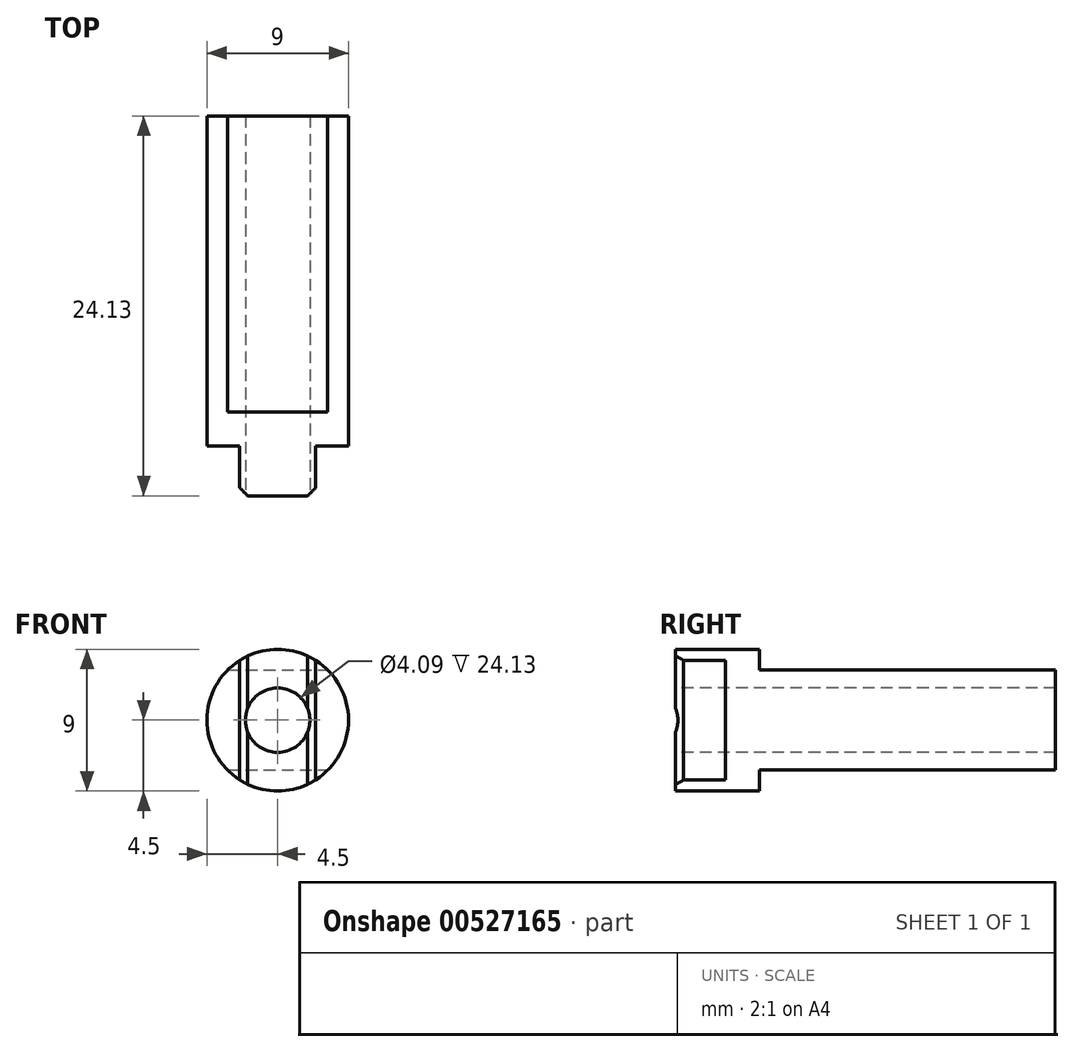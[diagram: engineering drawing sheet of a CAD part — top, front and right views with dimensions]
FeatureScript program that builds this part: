
annotation { "Feature Type Name" : "Feature", "Feature Type Description" : "" }
export const myFeature = defineFeature(function(context is Context, id is Id, definition is map)
    precondition{}
    {
        {
            var Q0;
            Q0=qCreatedBy(makeId("Front.planeOp"),FACE);
            var sketch = newSketch(context, id + "F0", { "sketchPlane" : qUnion([Q0])});
            skCircle(sketch, "E0", {"center": v(0, 0) * mm, "radius": 4.5 * mm});
            skSolve(sketch);
        }
        {
            var Q0;
            Q0=makeQuery(id+"F0.imprint","IMPRINT",FACE,{"disambiguationData":[TD([[makeQuery(id+"F0.imprint","IMPRINT",EDGE,{"derivedFrom":sQuery(id+"F0.wireOp",EDGE,"E0")}),1.0]])]});
            extrude(context, id + "F1", {"entities" : qUnion([Q0]), "oppositeDirection" : true, "depth" : 24.13 * mm, "offsetDistance" : 25.4 * mm});
        }
        {
            var Q0;
            Q0=qCreatedBy(makeId("Front.planeOp"),FACE);
            cPlane(context, id + "F2", {"entities" : qUnion([Q0]), "cplaneType" : CPlaneType.OFFSET, "offset" : 2.54 * mm, "width" : 152.4 * mm, "height" : 152.4 * mm});
        }
        {
            var Q0;
            Q0=qCreatedBy(id+"F2.planeOp",FACE);
            var sketch = newSketch(context, id + "F3", { "sketchPlane" : qUnion([Q0])});
            skLineSegment(sketch, "E1", {"start": v(-2.41, 9.78) * mm, "end": v(-2.41, -11.4) * mm});
            skLineSegment(sketch, "E2", {"start": v(-2.41, -11.4) * mm, "end": v(-8.76, -11.4) * mm});
            skLineSegment(sketch, "E3", {"start": v(-8.76, -11.4) * mm, "end": v(-8.76, 9.78) * mm});
            skLineSegment(sketch, "E4", {"start": v(-8.76, 9.78) * mm, "end": v(-2.41, 9.78) * mm});
            skLineSegment(sketch, "E5.MirrorCS", {"start": v(8.76, 9.78) * mm, "end": v(2.41, 9.78) * mm});
            skLineSegment(sketch, "E6.MirrorCS", {"start": v(8.76, -11.4) * mm, "end": v(8.76, 9.78) * mm});
            skLineSegment(sketch, "E7.MirrorCS", {"start": v(2.41, -11.4) * mm, "end": v(8.76, -11.4) * mm});
            skLineSegment(sketch, "E8.MirrorCS", {"start": v(2.41, 9.78) * mm, "end": v(2.41, -11.4) * mm});
            skSolve(sketch);
        }
        {
            var Q0;
            Q0=makeQuery(id+"F3.imprint","IMPRINT",FACE,{"disambiguationData":[TD([[makeQuery(id+"F3.imprint","IMPRINT",EDGE,{"derivedFrom":sQuery(id+"F3.wireOp",EDGE,"E1")}),-1.0]])]});
            var Q1;
            Q1=makeQuery(id+"F3.imprint","IMPRINT",FACE,{"disambiguationData":[TD([[makeQuery(id+"F3.imprint","IMPRINT",EDGE,{"derivedFrom":sQuery(id+"F3.wireOp",EDGE,"E5.MirrorCS")}),1.0]])]});
            extrude(context, id + "F4", {"entities" : qUnion([Q0, Q1]), "operationType" : NewBodyOperationType.REMOVE, "oppositeDirection" : true, "depth" : 5.7 * mm, "offsetDistance" : 25.4 * mm});
        }
        {
            var Q0;
            Q0=makeQuery(id+"F4.boolean.opBoolean","INTERSECT",EDGE,{"derivedFrom":[makeQuery(id+"F1.opExtrude","CAP_FACE",FACE,{"disambiguationData":[OSD([sQuery(id+"F0.wireOp",EDGE,"E0")])],"isStart":true}),makeQuery(id+"F4.opExtrude","SWEPT_FACE",FACE,{"disambiguationData":[OSD([sQuery(id+"F3.wireOp",EDGE,"E1")])]})]});
            var Q1;
            Q1=makeQuery(id+"F4.boolean.opBoolean","INTERSECT",EDGE,{"derivedFrom":[makeQuery(id+"F1.opExtrude","CAP_FACE",FACE,{"disambiguationData":[OSD([sQuery(id+"F0.wireOp",EDGE,"E0")])],"isStart":true}),makeQuery(id+"F4.opExtrude","SWEPT_FACE",FACE,{"disambiguationData":[OSD([sQuery(id+"F3.wireOp",EDGE,"E8.MirrorCS")])]})]});
            chamfer(context, id + "F5", {"entities" : qUnion([Q0, Q1]), "width" : 0.5 * mm, "tangentPropagation" : true});
        }
        {
            var Q0;
            Q0=makeQuery(id+"F1.opExtrude","CAP_FACE",FACE,{"disambiguationData":[OSD([sQuery(id+"F0.wireOp",EDGE,"E0")])],"isStart":false});
            cPlane(context, id + "F6", {"entities" : qUnion([Q0]), "cplaneType" : CPlaneType.OFFSET, "offset" : 2.54 * mm, "width" : 152.4 * mm, "height" : 152.4 * mm});
        }
        {
            var Q0;
            Q0=qCreatedBy(id+"F6.planeOp",FACE);
            var sketch = newSketch(context, id + "F7", { "sketchPlane" : qUnion([Q0])});
            skLineSegment(sketch, "E9", {"start": v(-9.23, 3.18) * mm, "end": v(9.2, 3.18) * mm});
            skLineSegment(sketch, "E10", {"start": v(9.2, 3.18) * mm, "end": v(9.2, 7.34) * mm});
            skLineSegment(sketch, "E11", {"start": v(9.2, 7.34) * mm, "end": v(-9.23, 7.34) * mm});
            skLineSegment(sketch, "E12", {"start": v(-9.23, 7.34) * mm, "end": v(-9.23, 3.18) * mm});
            skLineSegment(sketch, "E13.MirrorCS", {"start": v(9.2, -7.34) * mm, "end": v(-9.23, -7.34) * mm});
            skLineSegment(sketch, "E14.MirrorCS", {"start": v(-9.23, -7.34) * mm, "end": v(-9.23, -3.18) * mm});
            skLineSegment(sketch, "E15.MirrorCS", {"start": v(-9.23, -3.18) * mm, "end": v(9.2, -3.18) * mm});
            skLineSegment(sketch, "E16.MirrorCS", {"start": v(9.2, -3.18) * mm, "end": v(9.2, -7.34) * mm});
            skSolve(sketch);
        }
        {
            var Q0;
            Q0=makeQuery(id+"F7.imprint","IMPRINT",FACE,{"disambiguationData":[TD([[makeQuery(id+"F7.imprint","IMPRINT",EDGE,{"derivedFrom":sQuery(id+"F7.wireOp",EDGE,"E9")}),1.0]])]});
            var Q1;
            Q1=makeQuery(id+"F7.imprint","IMPRINT",FACE,{"disambiguationData":[TD([[makeQuery(id+"F7.imprint","IMPRINT",EDGE,{"derivedFrom":sQuery(id+"F7.wireOp",EDGE,"E13.MirrorCS")}),-1.0]])]});
            extrude(context, id + "F8", {"entities" : qUnion([Q0, Q1]), "operationType" : NewBodyOperationType.REMOVE, "oppositeDirection" : true, "depth" : 21.34 * mm, "offsetDistance" : 25.4 * mm});
        }
        {
            var Q0;
            Q0=makeQuery(id+"F1.opExtrude","CAP_FACE",FACE,{"disambiguationData":[OSD([sQuery(id+"F0.wireOp",EDGE,"E0")])],"isStart":true});
            var sketch = newSketch(context, id + "F9", { "sketchPlane" : qUnion([Q0])});
            skPoint(sketch, "E17", {"position": v(0, 0) * mm});
            skSolve(sketch);
        }
        {
            var Q0;
            Q0=sQuery(id+"F9.wireOp",VERTEX,"E17");
            var Q1;
            Q1=makeQuery(id+"F1.opExtrude","SWEPT_BODY",BODY,{"disambiguationData":[OSD([sQuery(id+"F0.wireOp",EDGE,"E0")])]});
            hole(context, id + "F10", {"style" : HoleStyle.SIMPLE, "endStyle" : HoleEndStyle.THROUGH, "holeDiameter" : 4.1 * mm, "isTappedThrough" : true, "tappedDepth" : 12.7 * mm, "tapClearance" : 3, "startFromSketch" : true, "locations" : qUnion([Q0]), "scope" : qUnion([Q1])});
        }
    });
